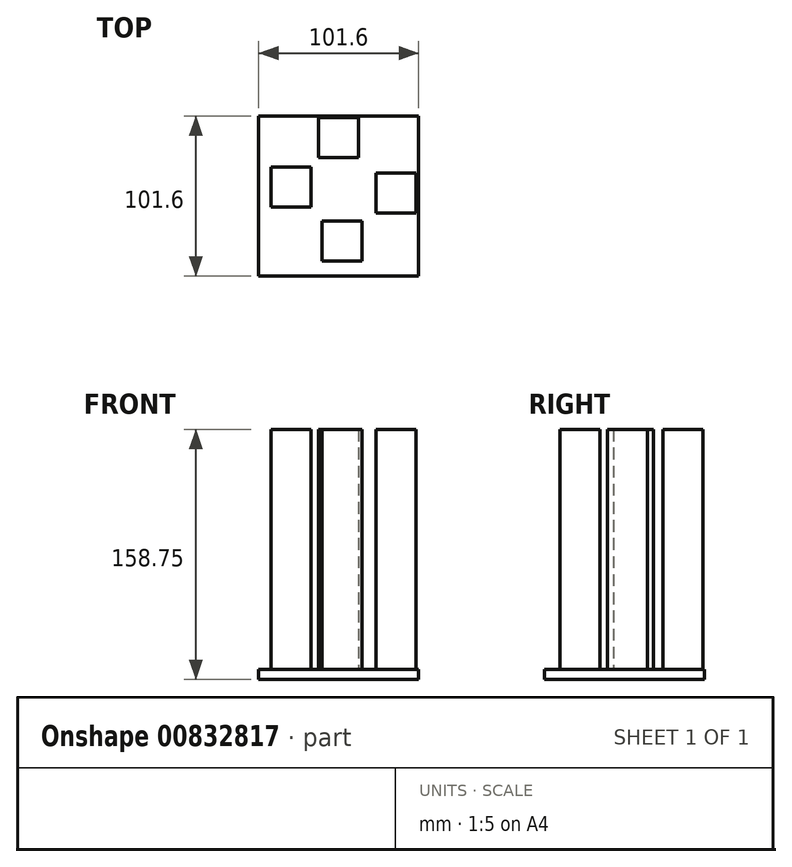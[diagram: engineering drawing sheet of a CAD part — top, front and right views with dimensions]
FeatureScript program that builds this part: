
annotation { "Feature Type Name" : "Feature", "Feature Type Description" : "" }
export const myFeature = defineFeature(function(context is Context, id is Id, definition is map)
    precondition{}
    {
        {
            var Q0;
            Q0=qCreatedBy(makeId("Top.planeOp"),FACE);
            var sketch = newSketch(context, id + "F0", { "sketchPlane" : qUnion([Q0])});
            skLineSegment(sketch, "E0.bottom", {"start": v(0, 0) * mm, "end": v(101.6, 0) * mm});
            skLineSegment(sketch, "E0.top", {"start": v(0, 101.6) * mm, "end": v(101.6, 101.6) * mm});
            skLineSegment(sketch, "E0.left", {"start": v(0, 0) * mm, "end": v(0, 101.6) * mm});
            skLineSegment(sketch, "E0.right", {"start": v(101.6, 0) * mm, "end": v(101.6, 101.6) * mm});
            skSolve(sketch);
        }
        {
            var Q0;
            Q0 = qSketchRegion(id + "F0", true);
            extrude(context, id + "F1", {"entities" : qUnion([Q0]), "depth" : 6.35 * mm, "offsetDistance" : 25.4 * mm});
        }
        {
            var Q0;
            Q0=makeQuery(id+"F1.opExtrude","CAP_FACE",FACE,{"disambiguationData":[OSD([sQuery(id+"F0.wireOp",EDGE,"E0.bottom"),sQuery(id+"F0.wireOp",EDGE,"E0.top"),sQuery(id+"F0.wireOp",EDGE,"E0.left"),sQuery(id+"F0.wireOp",EDGE,"E0.right")])],"isStart":false});
            var sketch = newSketch(context, id + "F2", { "sketchPlane" : qUnion([Q0])});
            skLineSegment(sketch, "E1.bottom", {"start": v(7.68, 69.13) * mm, "end": v(33.08, 69.13) * mm});
            skLineSegment(sketch, "E1.top", {"start": v(7.68, 43.73) * mm, "end": v(33.08, 43.73) * mm});
            skLineSegment(sketch, "E1.left", {"start": v(7.68, 69.13) * mm, "end": v(7.68, 43.73) * mm});
            skLineSegment(sketch, "E1.right", {"start": v(33.08, 69.13) * mm, "end": v(33.08, 43.73) * mm});
            skLineSegment(sketch, "E2.bottom", {"start": v(38.06, 100.5) * mm, "end": v(63.46, 100.5) * mm});
            skLineSegment(sketch, "E2.top", {"start": v(38.06, 75.1) * mm, "end": v(63.46, 75.1) * mm});
            skLineSegment(sketch, "E2.left", {"start": v(38.06, 100.5) * mm, "end": v(38.06, 75.1) * mm});
            skLineSegment(sketch, "E2.right", {"start": v(63.46, 100.5) * mm, "end": v(63.46, 75.1) * mm});
            skLineSegment(sketch, "E3.bottom", {"start": v(74.41, 65.4) * mm, "end": v(99.81, 65.4) * mm});
            skLineSegment(sketch, "E3.top", {"start": v(74.41, 40) * mm, "end": v(99.81, 40) * mm});
            skLineSegment(sketch, "E3.left", {"start": v(74.41, 65.4) * mm, "end": v(74.41, 40) * mm});
            skLineSegment(sketch, "E3.right", {"start": v(99.81, 65.4) * mm, "end": v(99.81, 40) * mm});
            skLineSegment(sketch, "E4.bottom", {"start": v(40.3, 35.01) * mm, "end": v(65.7, 35.01) * mm});
            skLineSegment(sketch, "E4.top", {"start": v(40.3, 9.61) * mm, "end": v(65.7, 9.61) * mm});
            skLineSegment(sketch, "E4.left", {"start": v(40.3, 35.01) * mm, "end": v(40.3, 9.61) * mm});
            skLineSegment(sketch, "E4.right", {"start": v(65.7, 35.01) * mm, "end": v(65.7, 9.61) * mm});
            skSolve(sketch);
        }
        {
            var Q0;
            Q0=makeQuery(id+"F2.imprint","IMPRINT",FACE,{"disambiguationData":[TD([[makeQuery(id+"F2.imprint","IMPRINT",EDGE,{"derivedFrom":sQuery(id+"F2.wireOp",EDGE,"E4.bottom")}),-1.0]])]});
            var Q1;
            Q1=makeQuery(id+"F2.imprint","IMPRINT",FACE,{"disambiguationData":[TD([[makeQuery(id+"F2.imprint","IMPRINT",EDGE,{"derivedFrom":sQuery(id+"F2.wireOp",EDGE,"E3.bottom")}),-1.0]])]});
            var Q2;
            Q2=makeQuery(id+"F2.imprint","IMPRINT",FACE,{"disambiguationData":[TD([[makeQuery(id+"F2.imprint","IMPRINT",EDGE,{"derivedFrom":sQuery(id+"F2.wireOp",EDGE,"E2.bottom")}),-1.0]])]});
            var Q3;
            Q3=makeQuery(id+"F2.imprint","IMPRINT",FACE,{"disambiguationData":[TD([[makeQuery(id+"F2.imprint","IMPRINT",EDGE,{"derivedFrom":sQuery(id+"F2.wireOp",EDGE,"E1.bottom")}),-1.0]])]});
            extrude(context, id + "F3", {"entities" : qUnion([Q0, Q1, Q2, Q3]), "operationType" : NewBodyOperationType.ADD, "depth" : 152.4 * mm, "offsetDistance" : 25.4 * mm});
        }
    });
